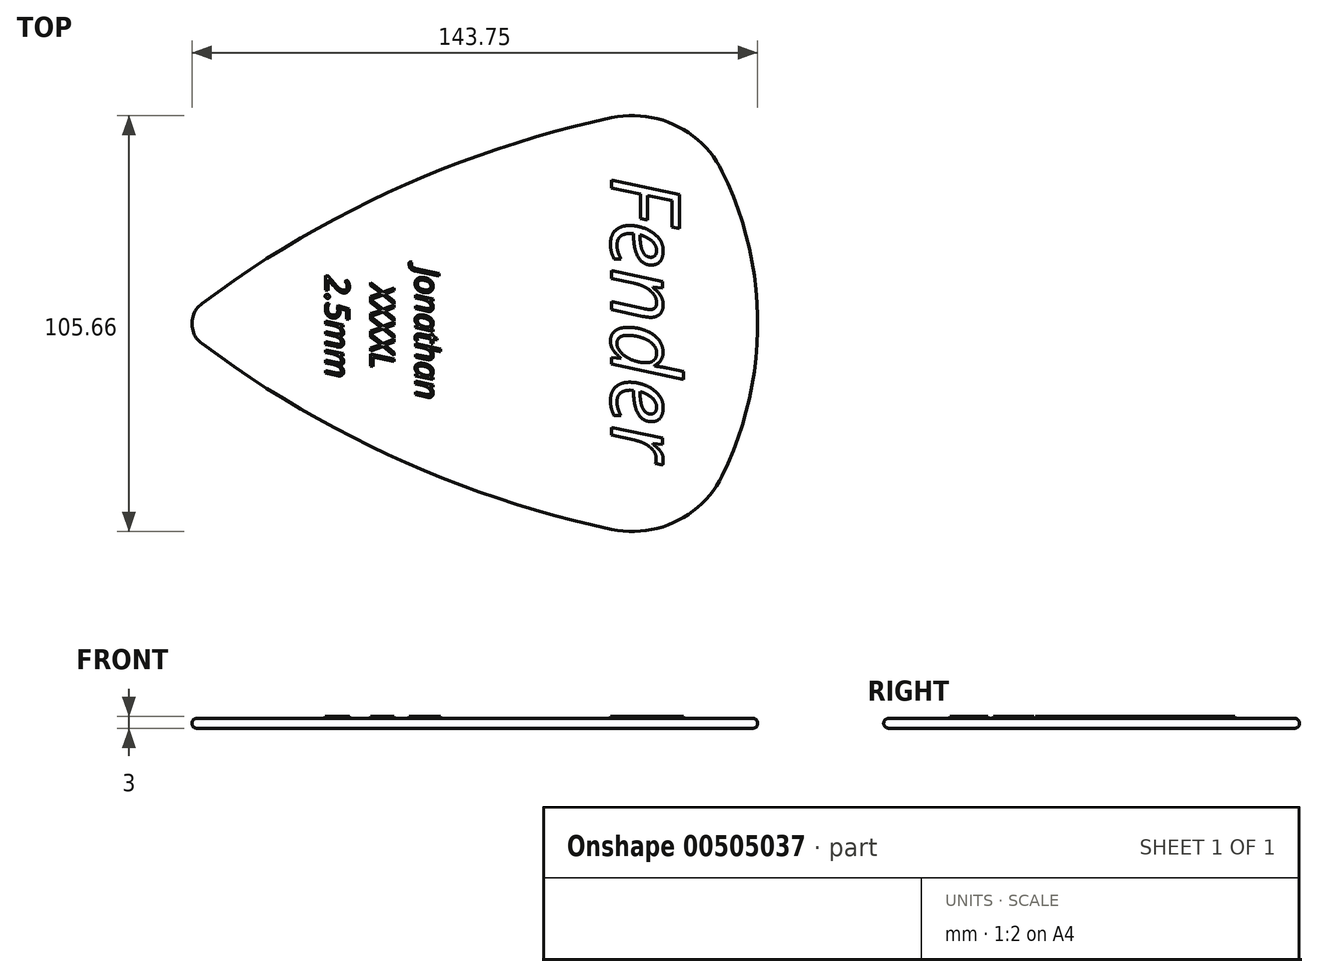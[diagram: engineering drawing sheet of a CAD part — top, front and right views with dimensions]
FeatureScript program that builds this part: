
annotation { "Feature Type Name" : "Feature", "Feature Type Description" : "" }
export const myFeature = defineFeature(function(context is Context, id is Id, definition is map)
    precondition{}
    {
        {
            var Q0;
            Q0=qCreatedBy(makeId("Top.planeOp"),FACE);
            var sketch = newSketch(context, id + "F0", { "sketchPlane" : qUnion([Q0])});
            skLineSegment(sketch, "E0", {"start": v(0, 0) * mm, "end": v(0, 55.37) * mm});
            skPoint(sketch, "E1.third.point", {"position": v(44.38, 12.77) * mm});
            skArc(sketch, "E2", {"start": v(-17.31, 52.27) * mm, "mid": v(-71.92, 34.31) * mm, "end": v(-121.41, 5.09) * mm});
            skPoint(sketch, "E2.third.point", {"position": v(253.23, -367.78) * mm});
            skArc(sketch, "E3.MirrorCS", {"start": v(-17.31, -52.27) * mm, "mid": v(-71.92, -34.31) * mm, "end": v(-121.41, -5.09) * mm});
            skLineSegment(sketch, "E4.MirrorCS", {"start": v(0, 0) * mm, "end": v(0, -55.37) * mm});
            skArc(sketch, "E5", {"start": v(10.76, -38.67) * mm, "mid": v(19.78, 0) * mm, "end": v(10.76, 38.67) * mm});
            skPoint(sketch, "E5.third.point", {"position": v(11.8, -36.5) * mm});
            skPoint(sketch, "E6.visualSharp", {"position": v(0, 55.37) * mm});
            skArc(sketch, "E6.filletArc", {"start": v(10.76, 38.67) * mm, "mid": v(-0.94, 50.29) * mm, "end": v(-17.31, 52.27) * mm});
            skPoint(sketch, "E7.visualSharp", {"position": v(-128.02, 0) * mm});
            skLineSegment(sketch, "E7.filletArc", {"start": v(-128.02, 0) * mm, "end": v(-128.02, 0) * mm});
            skPoint(sketch, "E8.visualSharp", {"position": v(0, -55.37) * mm});
            skArc(sketch, "E8.filletArc", {"start": v(-17.31, -52.27) * mm, "mid": v(-0.94, -50.29) * mm, "end": v(10.76, -38.67) * mm});
            skArc(sketch, "E9.filletArc", {"start": v(-121.41, 5.09) * mm, "mid": v(-123.97, 0) * mm, "end": v(-121.41, -5.09) * mm});
            skSolve(sketch);
        }
        {
            var Q0;
            Q0 = qSketchRegion(id + "F0", true);
            extrude(context, id + "F1", {"entities" : qUnion([Q0]), "depth" : -2.5 * mm});
        }
        {
            var Q0;
            Q0=qCreatedBy(makeId("Top.planeOp"),FACE);
            var sketch = newSketch(context, id + "F2", { "sketchPlane" : qUnion([Q0])});
            skText(sketch, "E10", { "text": "Fender", "fontName": "OpenSans-Italic.ttf"});
            skText(sketch, "E11", { "text": "Jonathan\n  XXXXL\n 2.5mm\n", "fontName": "OpenSans-Italic.ttf"});
            const initialGuessF2  = {"E10": [-0.0174, 0.03747, 0, -1, 0.0174], "E11": [-0.0672, 0.01437, 0, -1, 0.00603]};
            skSetInitialGuess(sketch, initialGuessF2);
            skSolve(sketch);
        }
        {
            var Q0;
            Q0 = qSketchRegion(id + "F2", true);
            extrude(context, id + "F3", {"entities" : qUnion([Q0]), "operationType" : NewBodyOperationType.ADD, "depth" : .5 * mm});
        }
        {
            var Q0;
            Q0=makeQuery(id+"F1.opExtrude","CAP_EDGE",EDGE,{"disambiguationData":[OSD([sQuery(id+"F0.wireOp",EDGE,"E3.MirrorCS")])],"isStart":true});
            var Q1;
            Q1=makeQuery(id+"F1.opExtrude","CAP_EDGE",EDGE,{"disambiguationData":[OSD([sQuery(id+"F0.wireOp",EDGE,"E3.MirrorCS")])],"isStart":false});
            fillet(context, id + "F4", {"entities" : qUnion([Q0, Q1]), "radius" : 1.25 * mm, "tangentPropagation" : true, "allowEdgeOverflow" : false});
        }
    });
